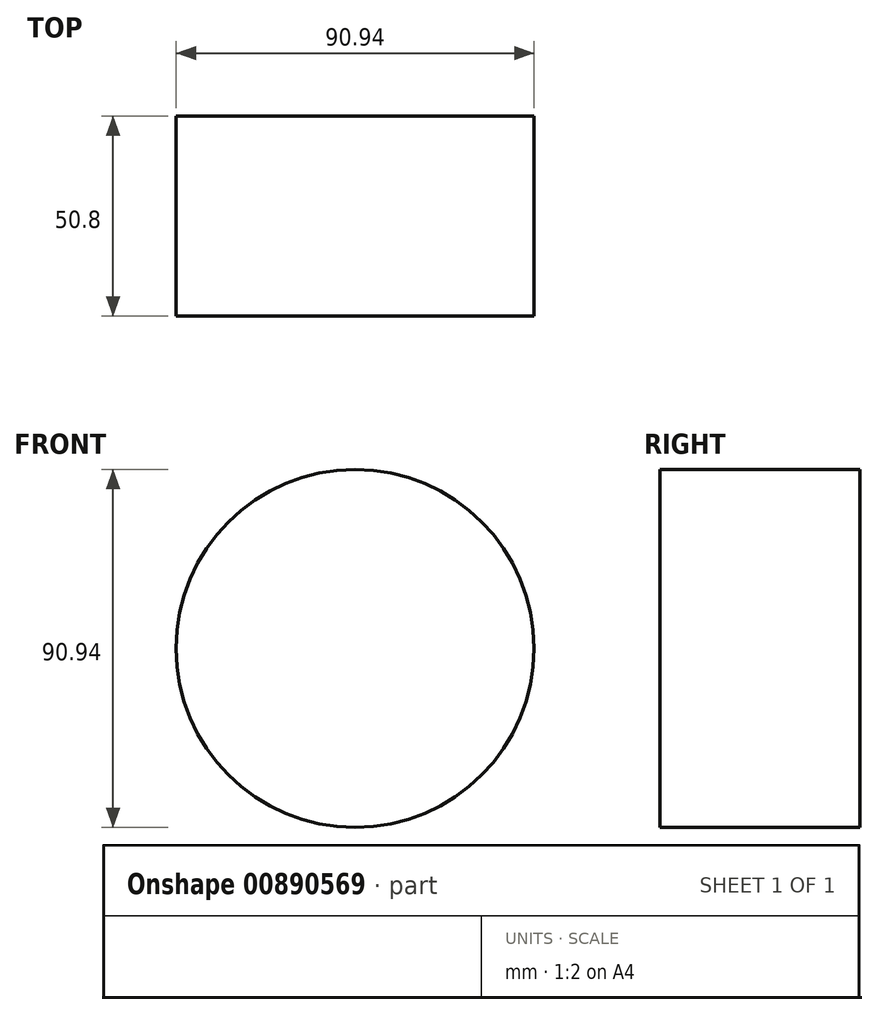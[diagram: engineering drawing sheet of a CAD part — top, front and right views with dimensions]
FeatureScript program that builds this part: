
annotation { "Feature Type Name" : "Feature", "Feature Type Description" : "" }
export const myFeature = defineFeature(function(context is Context, id is Id, definition is map)
    precondition{}
    {
        {
            var Q0;
            Q0=qCreatedBy(makeId("Front.planeOp"),FACE);
            var sketch = newSketch(context, id + "F0", { "sketchPlane" : qUnion([Q0])});
            skCircle(sketch, "E0", {"center": v(111.5, 0) * mm, "radius": 45.47 * mm});
            skSolve(sketch);
        }
        {
            var Q0;
            Q0 = qSketchRegion(id + "F0", true);
            extrude(context, id + "F1", {"entities" : qUnion([Q0]), "depth" : 25.4 * mm, "offsetDistance" : 25.4 * mm, "hasSecondDirection" : true, "secondDirectionOppositeDirection" : true, "secondDirectionDepth" : 25.4 * mm});
        }
    });
